FCSTD DOCUMENT  (FreeCAD 0.21R33694 (Git))
Label: box_assembly
License: All rights reserved
LicenseURL: http://en.wikipedia.org/wiki/All_rights_reserved
objects: App::Link×14, App::Part×1
EXTERNAL_REF file=../master_kumiko_box.FCStd obj=Spreadsheet
EXTERNAL_REF file=../parts/box/kumiko_box_floor.FCStd obj=Body032
EXTERNAL_REF file=../parts/box/kumiko_box_wall_long.FCStd obj=Body009
EXTERNAL_REF file=../parts/box/kumiko_box_wall_short.FCStd obj=Body009
EXTERNAL_REF file=../parts/box/kumiko_box_key_miter.FCStd obj=Body014

FEATURE [App::Link] Link  label="SpreadSheet"
  LinkedObject = -> <external ../master_kumiko_box.FCStd>#Spreadsheet
FEATURE [App::Link] Link001  label="floor"
  LinkPlacement = pos=(5.75,5.75,0) rot=(0,0,1;0rad)
  LinkedObject = -> <external ../parts/box/kumiko_box_floor.FCStd>#Body032
  Placement = pos=(5.75,5.75,0) rot=(0,0,1;0rad)
  expr: .Placement.Base.x = <<SpreadSheet>>.box_thickness / 2
  expr: .Placement.Base.y = <<SpreadSheet>>.box_thickness / 2
FEATURE [App::Link] Link002  label="wall_front"
  LinkPlacement = pos=(130,0,2) rot=(0,0,1;1.5708rad)
  LinkedObject = -> <external ../parts/box/kumiko_box_wall_long.FCStd>#Body009
  Placement = pos=(130,0,2) rot=(0,0,1;1.5708rad)
  expr: .Placement.Base.x = <<SpreadSheet>>.box_length
  expr: .Placement.Base.z = <<SpreadSheet>>.floor_edge
  expr: .Placement.Rotation.Angle = 90
FEATURE [App::Link] Link003  label="wall_left"
  LinkPlacement = pos=(0,0,2) rot=(0,0,1;0rad)
  LinkedObject = -> <external ../parts/box/kumiko_box_wall_short.FCStd>#Body009
  Placement = pos=(0,0,2) rot=(0,0,1;0rad)
  expr: .Placement.Base.x = 0
  expr: .Placement.Base.y = 0
  expr: .Placement.Base.z = <<SpreadSheet>>.floor_edge
FEATURE [App::Link] Link004  label="wall_back"
  LinkPlacement = pos=(0,75,2) rot=(0,0,1;4.71239rad)
  LinkedObject = -> <external ../parts/box/kumiko_box_wall_long.FCStd>#Body009
  Placement = pos=(0,75,2) rot=(0,0,1;4.71239rad)
  expr: .Placement.Base.x = 0
  expr: .Placement.Base.y = <<SpreadSheet>>.box_width
  expr: .Placement.Base.z = <<SpreadSheet>>.floor_edge
  expr: .Placement.Rotation.Angle = 270
FEATURE [App::Link] Link005  label="wall_right"
  LinkPlacement = pos=(130,75,2) rot=(0,0,1;3.14159rad)
  LinkedObject = -> <external ../parts/box/kumiko_box_wall_short.FCStd>#Body009
  Placement = pos=(130,75,2) rot=(0,0,1;3.14159rad)
  expr: .Placement.Base.x = <<SpreadSheet>>.box_length
  expr: .Placement.Base.y = <<SpreadSheet>>.box_width
  expr: .Placement.Base.z = <<SpreadSheet>>.floor_edge
  expr: .Placement.Rotation.Angle = 180
FEATURE [App::Link] Link006  label="miter_key_a"
  LinkPlacement = pos=(0,0,9) rot=(0,0,1;0rad)
  LinkedObject = -> <external ../parts/box/kumiko_box_key_miter.FCStd>#Body014
  Placement = pos=(0,0,9) rot=(0,0,1;0rad)
  expr: .Placement.Base.x = 0
  expr: .Placement.Base.z = <<SpreadSheet>>.floor_edge + (<<SpreadSheet>>.lid_height - <<SpreadSheet>>.kumiko_thickness) / 2
FEATURE [App::Link] Link007  label="miter_key_b"
  LinkPlacement = pos=(0,0,33) rot=(0,0,1;0rad)
  LinkedObject = -> <external ../parts/box/kumiko_box_key_miter.FCStd>#Body014
  Placement = pos=(0,0,33) rot=(0,0,1;0rad)
  expr: .Placement.Base.z = <<SpreadSheet>>.box_height - <<SpreadSheet>>.lid_height - (<<SpreadSheet>>.lid_height + <<SpreadSheet>>.kumiko_thickness) / 2
FEATURE [App::Link] Link008  label="miter_key_c"
  LinkPlacement = pos=(130,0,9) rot=(0,0,1;1.5708rad)
  LinkedObject = -> <external ../parts/box/kumiko_box_key_miter.FCStd>#Body014
  Placement = pos=(130,0,9) rot=(0,0,1;1.5708rad)
  expr: .Placement.Base.x = <<SpreadSheet>>.box_length
  expr: .Placement.Base.z = <<SpreadSheet>>.floor_edge + (<<SpreadSheet>>.lid_height - <<SpreadSheet>>.kumiko_thickness) / 2
  expr: .Placement.Rotation.Angle = 90
FEATURE [App::Link] Link009  label="miter_key_d"
  LinkPlacement = pos=(130,0,33) rot=(0,0,1;1.5708rad)
  LinkedObject = -> <external ../parts/box/kumiko_box_key_miter.FCStd>#Body014
  Placement = pos=(130,0,33) rot=(0,0,1;1.5708rad)
  expr: .Placement.Base.x = <<SpreadSheet>>.box_length
  expr: .Placement.Base.z = <<SpreadSheet>>.box_height - <<SpreadSheet>>.lid_height - (<<SpreadSheet>>.lid_height + <<SpreadSheet>>.kumiko_thickness) / 2
  expr: .Placement.Rotation.Angle = 90
FEATURE [App::Link] Link010  label="miter_key_e"
  LinkPlacement = pos=(130,75,9) rot=(0,0,1;3.14159rad)
  LinkedObject = -> <external ../parts/box/kumiko_box_key_miter.FCStd>#Body014
  Placement = pos=(130,75,9) rot=(0,0,1;3.14159rad)
  expr: .Placement.Base.x = <<SpreadSheet>>.box_length
  expr: .Placement.Base.y = <<SpreadSheet>>.box_width
  expr: .Placement.Base.z = <<SpreadSheet>>.floor_edge + (<<SpreadSheet>>.lid_height - <<SpreadSheet>>.kumiko_thickness) / 2
FEATURE [App::Link] Link011  label="miter_key_f"
  LinkPlacement = pos=(130,75,33) rot=(0,0,1;3.14159rad)
  LinkedObject = -> <external ../parts/box/kumiko_box_key_miter.FCStd>#Body014
  Placement = pos=(130,75,33) rot=(0,0,1;3.14159rad)
  expr: .Placement.Base.x = <<SpreadSheet>>.box_length
  expr: .Placement.Base.y = <<SpreadSheet>>.box_width
  expr: .Placement.Base.z = <<SpreadSheet>>.box_height - <<SpreadSheet>>.lid_height - (<<SpreadSheet>>.lid_height + <<SpreadSheet>>.kumiko_thickness) / 2
FEATURE [App::Link] Link012  label="miter_key_g"
  LinkPlacement = pos=(0,75,9) rot=(0,0,1;4.71239rad)
  LinkedObject = -> <external ../parts/box/kumiko_box_key_miter.FCStd>#Body014
  Placement = pos=(0,75,9) rot=(0,0,1;4.71239rad)
  expr: .Placement.Base.y = <<SpreadSheet>>.box_width
  expr: .Placement.Base.z = <<SpreadSheet>>.floor_edge + (<<SpreadSheet>>.lid_height - <<SpreadSheet>>.kumiko_thickness) / 2
FEATURE [App::Link] Link013  label="miter_key_h"
  LinkPlacement = pos=(0,75,33) rot=(0,0,1;4.71239rad)
  LinkedObject = -> <external ../parts/box/kumiko_box_key_miter.FCStd>#Body014
  Placement = pos=(0,75,33) rot=(0,0,1;4.71239rad)
  expr: .Placement.Base.y = <<SpreadSheet>>.box_width
  expr: .Placement.Base.z = <<SpreadSheet>>.box_height - <<SpreadSheet>>.lid_height - (<<SpreadSheet>>.lid_height + <<SpreadSheet>>.kumiko_thickness) / 2
FEATURE [App::Part] Part  label="box"
  Group = -> [Link001,Link004,Link003,Link006,Link007,Link008,Link005,Link002,Link009,Link010,Link011,Link012,Link013]
  Origin = -> Origin

RESOLVED EXTERNAL PARTS (link-assembly join: the EXTERNAL_REF files above that resolve inside this repo's crawl, each included once):
---- part ../master_kumiko_box.FCStd = doc fcstd_d57fc246fb5e ----
FCSTD DOCUMENT  (FreeCAD 0.21R33771 (Git))
Label: master_kumiko_box
License: All rights reserved
LicenseURL: https://en.wikipedia.org/wiki/All_rights_reserved
objects: App::Link×3, App::Part×2, Spreadsheet::Sheet×1
EXTERNAL_REF file=assembly/box_assembly.FCStd obj=Part
EXTERNAL_REF file=assembly/lid_assembly.FCStd obj=Part
EXTERNAL_REF file=assembly/kumiko_assembly.FCStd obj=Part001

FEATURE [Spreadsheet::Sheet] Spreadsheet  label="SpreadSheet"
  cells = A1='name; B1='value; C1='calc (y/n); A2='box_length; B2(box_length)=130; C2='n; A3='box_width; B3(box_width)==B2 / 2 + B5 - B13 / 2; C3='n; A4='box_height; B4(box_height)=60; C4='y; A5='box_thickness; B5(box_thickness)=11.5; C5='y; A7='lid_height; B7(lid_height)==B8 * 17 / 8.5; C7='y; A8='lid_frame_width; B8(lid_frame_width)==B5 - B13; C8='y; A9='lid_lip_width; B9(lid_lip_width)==B5 - B8; C9='y; A10='lid_lip_height; B10(lid_lip_hight)=3; C10='y; A12='kumiko_hight; B12(kumiko_hight)==B7 * 11 / 17; C12='y; A13='kumiko_thickness; B13(kumiko_thickness)=3; C13='n; A14='kumiko_grid_size; B14(kumiko_grid_size)==(B2 - 2 * B8 - B13) / 4; C14='y; A16='box_wall_height; B16(box_wall_height)==B4 - B7 - B18; C16='y; A18='floor_edge; B18(floor_edge)=2; C18='n; A20='cnc_spacing; B20(cnc_spacing)=0; C20='y
FEATURE [App::Link] Link  label="box"
  LinkedObject = -> <external assembly/box_assembly.FCStd>#Part
FEATURE [App::Link] Link001  label="lid"
  LinkPlacement = pos=(0,0,43) rot=(0,0,1;0rad)
  LinkedObject = -> <external assembly/lid_assembly.FCStd>#Part
  Placement = pos=(0,0,43) rot=(0,0,1;0rad)
  expr: .Placement.Base.z = <<SpreadSheet>>.box_height - <<SpreadSheet>>.lid_height
FEATURE [App::Link] Link002  label="kumiko_assembly"
  LinkPlacement = pos=(8.5,8.5,49) rot=(0,0,1;0rad)
  LinkedObject = -> <external assembly/kumiko_assembly.FCStd>#Part001
  Placement = pos=(8.5,8.5,49) rot=(0,0,1;0rad)
  expr: .Placement.Base.x = <<SpreadSheet>>.lid_frame_width
  expr: .Placement.Base.y = <<SpreadSheet>>.lid_frame_width
  expr: .Placement.Base.z = <<SpreadSheet>>.box_height - Spreadsheet.kumiko_hight
FEATURE [App::Part] Part  label="lid_complete"
  Group = -> [Link002,Link001]
  Origin = -> Origin
FEATURE [App::Part] Part001  label="kumiko_box_complete"
  Group = -> [Part,Link]
  Origin = -> Origin001
---- part ../parts/box/kumiko_box_floor.FCStd = doc fcstd_ba5c48548d76 ----
FCSTD DOCUMENT  (FreeCAD 0.21R33771 (Git))
Label: kumiko_box_floor
License: All rights reserved
LicenseURL: https://en.wikipedia.org/wiki/All_rights_reserved
objects: Path::FeaturePython×4, Part::FeaturePython×3, App::DocumentObjectGroup×3, Sketcher::SketchObject×2, PartDesign::Pad×2, App::Link×1, PartDesign::Body×1, App::FeaturePython×1, Mesh::FeaturePython×1
note: 12 computed .brp shape members not serialized (recipe doc carries the construction recipe); baked Part::Feature solids carry a one-line shape summary decoded from their .brp
EXTERNAL_REF file=../../master_kumiko_box.FCStd obj=Spreadsheet

FEATURE [App::Link] Link  label="SpreadSheet"
  LinkedObject = -> <external ../../master_kumiko_box.FCStd>#Spreadsheet
FEATURE [Sketcher::SketchObject] Sketch  label="ground_pad_drawing"
  FullyConstrained = true
  MapMode = 5
  Support = -> [XY_Plane043]
  expr: Constraints[10] = <<SpreadSheet>>.box_width - 2 * <<SpreadSheet>>.box_thickness
  expr: Constraints[11] = <<SpreadSheet>>.box_length - 2 * <<SpreadSheet>>.box_thickness
  expr: Constraints[8] = <<SpreadSheet>>.box_thickness / 2
  expr: Constraints[9] = <<SpreadSheet>>.box_thickness / 2
  sketch-geometry (4):
    g0: LineSegment StartX=5.75 StartY=5.75 StartZ=0 EndX=112.75 EndY=5.75 EndZ=0
    g1: LineSegment StartX=112.75 StartY=5.75 StartZ=0 EndX=112.75 EndY=57.75 EndZ=0
    g2: LineSegment StartX=112.75 StartY=57.75 StartZ=0 EndX=5.75 EndY=57.75 EndZ=0
    g3: LineSegment StartX=5.75 StartY=57.75 StartZ=0 EndX=5.75 EndY=5.75 EndZ=0
  constraints (12):
    c: Coincident(g0,g1)
    c: Coincident(g1,g2)
    c: Coincident(g2,g3)
    c: Coincident(g3,g0)
    c: Horizontal(g0)
    c: Horizontal(g2)
    c: Vertical(g1)
    c: Vertical(g3)
    c: DistanceX(g-1,g0) = 5.75
    c: DistanceY(g-1,g0) = 5.75
    c: DistanceY(g3,g3) = 52
    c: DistanceX(g2,g2) = 107
FEATURE [PartDesign::Pad] Pad  label="ground_pad"
  Direction = (0,0,1)
  Length = 5.75
  Length2 = 10
  Profile = -> Sketch
  ReferenceAxis = -> Sketch [N_Axis]
  Type = 0
  expr: Length = <<SpreadSheet>>.box_thickness / 2
FEATURE [Sketcher::SketchObject] Sketch001  label="half_lap_joint_drawing"
  FullyConstrained = true
  MapMode = 5
  Placement = pos=(0,0,5.75) rot=(0,0,1;0rad)
  Support = -> [Pad]
  expr: Constraints[10] = <<SpreadSheet>>.box_width - <<SpreadSheet>>.box_thickness
  expr: Constraints[9] = <<SpreadSheet>>.box_length - <<SpreadSheet>>.box_thickness
  sketch-geometry (4):
    g0: LineSegment StartX=0 StartY=0 StartZ=0 EndX=118.5 EndY=0 EndZ=0
    g1: LineSegment StartX=118.5 StartY=0 StartZ=0 EndX=118.5 EndY=63.5 EndZ=0
    g2: LineSegment StartX=118.5 StartY=63.5 StartZ=0 EndX=0 EndY=63.5 EndZ=0
    g3: LineSegment StartX=0 StartY=63.5 StartZ=0 EndX=0 EndY=0 EndZ=0
  constraints (12):
    c: Coincident(g0,g1)
    c: Coincident(g1,g2)
    c: Coincident(g2,g3)
    c: Coincident(g3,g0)
    c: Horizontal(g0)
    c: Horizontal(g2)
    c: Vertical(g1)
    c: Vertical(g3)
    c: PointOnObject(g0,g-1)
    c: DistanceX(g2,g2) = 118.5
    c: DistanceY(g1,g1) = 63.5
    c: DistanceX(g-1,g0) = 0
FEATURE [PartDesign::Pad] Pad001  label="half_lap_jount"
  BaseFeature = -> Pad
  Direction = (0,0,1)
  Length = 5.75
  Length2 = 10
  Profile = -> Sketch001
  ReferenceAxis = -> Sketch001 [N_Axis]
  Type = 0
  expr: Length = <<SpreadSheet>>.box_thickness / 2
FEATURE [PartDesign::Body] Body032  label="floor_body"
  Group = -> [Sketch,Pad,Sketch001,Pad001]
  Origin = -> Origin043
  Placement = pos=(0,63.5,0) rot=(1,0,0;3.14159rad)
  Tip = -> Pad001
  expr: .Placement.Base.x = 0
  expr: .Placement.Base.y = <<SpreadSheet>>.box_width - <<SpreadSheet>>.box_thickness
  expr: .Placement.Base.z = 0
FEATURE [App::FeaturePython] SetupSheet  # Path/CAM operation (typed FeaturePython)
  ClearanceHeightExpression = OpStockZMax+SetupSheet.ClearanceHeightOffset
  ClearanceHeightOffset = 5
  CoolantMode = 0
  CoolantModes = None | Flood | Mist
  FinalDepthExpression = OpFinalDepth
  HorizRapid = 0
  SafeHeightExpression = OpStockZMax+SetupSheet.SafeHeightOffset
  SafeHeightOffset = 3
  StartDepthExpression = OpStartDepth
  StepDownExpression = OpToolDiameter
  VertRapid = 0
FEATURE [Part::FeaturePython] Clone  label="Model-floor_body"  # Draft clone (typed FeaturePython)
  AttacherType = Attacher::AttachEngine3D
  Fuse = false
  Objects = -> [Body032]
  PathResource = Model
  Placement = pos=(0,63.5,0) rot=(1,0,0;3.14159rad)
  Scale = (1,1,1)
FEATURE [App::DocumentObjectGroup] Model
  Group = -> [Clone]
FEATURE [Part::FeaturePython] Stock  # WARN: FeaturePython — macro-defined, semantics opaque (R4)
  Base = -> Model
  ExtXneg = 3
  ExtXpos = 3
  ExtYneg = 3
  ExtYpos = 3
  ExtZneg = 0
  ExtZpos = 0
  Placement = pos=(0,0,-11.5) rot=(0,0,1;0rad)
  StockType = FromBase
FEATURE [Part::FeaturePython] ToolBit001  label="FREES_5mm"  # Path/CAM toolbit (typed FeaturePython)
  BitPropertyNames = Chipload | CuttingEdgeHeight | Diameter | Flutes | Length | Material | ShankDiameter | SpindleDirection
  BitShape = /Applications/FreeCAD.app/Contents/Resources/Mod/Path/Tools/Shape/endmill.fcstd
  Chipload = 0
  CuttingEdgeHeight = 13
  Diameter = 5
  File = <userpath>/Library/Application Support/FreeCAD/Macro/FREES_5mm.fctb
  Flutes = 0
  Length = 57
  Material = 0
  ShankDiameter = 6
  ShapeName = endmill
  SpindleDirection = 0
FEATURE [Path::FeaturePython] FREES_5mm  label="FREES_5mm001"  # Path/CAM operation (typed FeaturePython)
  HorizFeed = 1
  HorizRapid = 0
  SpindleDir = 0
  SpindleSpeed = 4
  Tool = -> ToolBit001
  ToolNumber = 2
  VertFeed = 0.5
  VertRapid = 0
  expr: HorizRapid = SetupSheet.HorizRapid
  expr: VertRapid = SetupSheet.VertRapid
FEATURE [App::DocumentObjectGroup] Tools
  Group = -> [FREES_5mm]
FEATURE [Path::FeaturePython] Profile  # Path/CAM operation (typed FeaturePython)
  Active = true
  AreaParams:
    Tolerance = 1e-07
    FitArcs = True
    Simplify = False
    CleanDistance = 0.0
    Accuracy = 0.01
    Unit = 1.0
    MinArcPoints = 4
    MaxArcPoints = 100
    ClipperScale = 10000000.0
    Fill = 0
    Coplanar = 0
    Reorient = True
    Outline = False
    Explode = False
    OpenMode = 0
    Deflection = 0.01
    SubjectFill = 0
    ClipFill = 0
    Offset = 2.5
    ExtraPass = 0
    Stepover = 0.0
    LastStepover = 0.0
    JoinType = 0
    EndType = 0
    MiterLimit = 2.0
    RoundPrecision = 0.0
    PocketMode = 0
    ToolRadius = 1.0
    PocketExtraOffset = 0.0
    PocketStepover = 0.0
    PocketLastStepover = 0.0
    FromCenter = False
    Angle = 45.0
    AngleShift = 0.0
    Shift = 0.0
    Thicken = False
    SectionCount = -1
    Stepdown = 1.0
    SectionOffset = 0.0
    SectionTolerance = 1e-07
    SectionMode = 2
    Project = False
  Base = -> [Clone]
  ClearanceHeight = 5
  CoolantMode = 0
  CycleTime = 01:16:33
  Direction = 1
  FinalDepth = -11.5
  HandleMultipleFeatures = 0
  JoinType = 0
  MiterLimit = 0.1
  OffsetExtra = 0
  OpFinalDepth = -11.5
  OpStartDepth = 7.1e-15
  OpStockZMax = 0
  OpStockZMin = -11.5
  OpToolDiameter = 5
  PathParams = {'orientation': 0, 'feedrate': 1.0, 'feedrate_v': 0.5, 'verbose': True, 'resume_height': 3.0, 'retraction': 5.0, 'return_end': True, 'preamble': False, 'start': Vector (0.0, 0.0, 0.0)}
  SafeHeight = 3
  Side = 0
  SplitArcs = false
  StartDepth = 7.1e-15
  StartPoint = (0,0,0)
  StepDown = 1
  ToolController = -> FREES_5mm
  UseComp = true
  UseStartPoint = true
  processCircles = false
  processHoles = false
  processPerimeter = true
  expr: ClearanceHeight = OpStockZMax + SetupSheet.ClearanceHeightOffset
  expr: FinalDepth = OpFinalDepth
  expr: SafeHeight = OpStockZMax + SetupSheet.SafeHeightOffset
  expr: StartDepth = OpStartDepth
  expr: StepDown = 1
FEATURE [Path::FeaturePython] Pocket_Shape  # Path/CAM operation (typed FeaturePython)
  Active = true
  AreaParams:
    Tolerance = 1e-07
    FitArcs = True
    Simplify = False
    CleanDistance = 0.0
    Accuracy = 0.01
    Unit = 1.0
    MinArcPoints = 4
    MaxArcPoints = 100
    ClipperScale = 10000000.0
    Fill = 0
    Coplanar = 0
    Reorient = True
    Outline = False
    Explode = False
    OpenMode = 0
    Deflection = 0.01
    SubjectFill = 0
    ClipFill = 0
    Offset = 0.0
    ExtraPass = 0
    Stepover = 0.0
    LastStepover = 0.0
    JoinType = 0
    EndType = 0
    MiterLimit = 2.0
    RoundPrecision = 0.0
    PocketMode = 2
    ToolRadius = 2.5
    PocketExtraOffset = 0.0
    PocketStepover = 2.0
    PocketLastStepover = 0.0
    FromCenter = True
    Angle = 45.0
    AngleShift = 0.0
    Shift = 0.0
    Thicken = False
    SectionCount = -1
    Stepdown = 1.0
    SectionOffset = 0.0
    SectionTolerance = 1e-07
    SectionMode = 2
    Project = False
  Base = -> [Clone]
  ClearanceHeight = 5
  CoolantMode = 0
  CutMode = 0
  CycleTime = 02:11:12
  ExtensionCorners = true
  ExtensionFeature = -> [Clone]
  ExtensionLengthDefault = 2.5
  ExtraOffset = 0
  FinalDepth = -5.75
  FinishDepth = 0.5
  KeepToolDown = false
  MinTravel = false
  OffsetPattern = 1
  OpFinalDepth = -5.75
  OpStartDepth = 7.1e-15
  OpStockZMax = 0
  OpStockZMin = -11.5
  OpToolDiameter = 5
  PathParams = {'orientation': 1, 'feedrate': 1.0, 'feedrate_v': 0.5, 'verbose': True, 'resume_height': 3.0, 'retraction': 5.0, 'return_end': True, 'preamble': False, 'start': Vector (0.0, 0.0, 0.0)}
  PocketLastStepOver = 0
  SafeHeight = 3
  SplitArcs = false
  StartAt = 0
  StartDepth = 7.1e-15
  StartPoint = (0,0,0)
  StepDown = 1
  StepOver = 40
  ToolController = -> FREES_5mm
  UseOutline = false
  UseStartPoint = true
  ZigZagAngle = 45
  expr: ClearanceHeight = OpStockZMax + SetupSheet.ClearanceHeightOffset
  expr: ExtensionLengthDefault = OpToolDiameter / 2
  expr: FinalDepth = OpFinalDepth
  expr: SafeHeight = OpStockZMax + SetupSheet.SafeHeightOffset
  expr: StartDepth = OpStartDepth
  expr: StepDown = 1
FEATURE [App::DocumentObjectGroup] Operations
  Group = -> [Profile,Pocket_Shape]
FEATURE [Path::FeaturePython] Job  # Path/CAM operation (typed FeaturePython)
  CycleTime = 03:27:45
  Fixtures = G54
  GeometryTolerance = 0.01
  JobType = 0
  LastPostProcessDate = 2024-03-20 12:44:18.073578
  LastPostProcessOutput = <userpath>/Documents/jewelry_kumiko_box/cnc/bin/kumiko_floor-0.nc
  Model = -> Model
  Operations = -> Operations
  OrderOutputBy = 0
  PostProcessor = 14
  PostProcessorOutputFile = <userpath>/Documents/jewelry_kumiko_box/cnc/bin/kumiko_floor.nc
  SetupSheet = -> SetupSheet
  SplitOutput = true
  Stock = -> Stock
  Tools = -> Tools
FEATURE [Mesh::FeaturePython] CutMaterial  # WARN: FeaturePython — macro-defined, semantics opaque (R4)
---- part ../parts/box/kumiko_box_key_miter.FCStd = doc fcstd_dc4a3549b709 ----
FCSTD DOCUMENT  (FreeCAD 0.21R33694 (Git))
Label: kumiko_box_key_miter
License: All rights reserved
LicenseURL: https://en.wikipedia.org/wiki/All_rights_reserved
objects: Sketcher::SketchObject×1, PartDesign::Pad×1, PartDesign::Body×1, App::Link×1
note: 4 computed .brp shape members not serialized (recipe doc carries the construction recipe); baked Part::Feature solids carry a one-line shape summary decoded from their .brp
EXTERNAL_REF file=../../master_kumiko_box.FCStd obj=Spreadsheet

FEATURE [Sketcher::SketchObject] Sketch027  label="miter_key_drawing"
  FullyConstrained = true
  MapMode = 5
  Support = -> [XY_Plane016]
  expr: Constraints[6] = <<SpreadSheet>>.lid_frame_width
  expr: Constraints[7] = 0
  expr: Constraints[8] = 0
  sketch-geometry (3):
    g0: LineSegment StartX=0 StartY=8.5 StartZ=0 EndX=0 EndY=0 EndZ=0
    g1: LineSegment StartX=0 StartY=0 StartZ=0 EndX=8.5 EndY=0 EndZ=0
    g2: LineSegment StartX=8.5 StartY=0 StartZ=0 EndX=0 EndY=8.5 EndZ=0
  constraints (9):
    c: Vertical(g0)
    c: Coincident(g1,g0)
    c: Horizontal(g1)
    c: Coincident(g2,g1)
    c: Coincident(g2,g0)
    c: Equal(g0,g1)
    c: DistanceX(g1,g1) = 8.5
    c: DistanceX(g-1,g0) = 0
    c: DistanceY(g0,g-1) = 0
FEATURE [PartDesign::Pad] Pad012  label="miter_key_extrude"
  Direction = (0,0,1)
  Length = 3
  Length2 = 10
  Profile = -> Sketch027
  ReferenceAxis = -> Sketch027 [N_Axis]
  Type = 0
  expr: Length = <<SpreadSheet>>.kumiko_thickness
FEATURE [PartDesign::Body] Body014  label="miter_key"
  Group = -> [Sketch027,Pad012]
  Origin = -> Origin016
  Tip = -> Pad012
  expr: .Placement.Base.x = 0
  expr: .Placement.Base.y = 0
  expr: .Placement.Base.z = 0
  expr: .Placement.Rotation.Angle = 0
  expr: .Placement.Rotation.Axis.x = 0
  expr: .Placement.Rotation.Axis.y = 0
  expr: .Placement.Rotation.Axis.z = 1
FEATURE [App::Link] Link  label="SpreadSheet"
  LinkedObject = -> <external ../../master_kumiko_box.FCStd>#Spreadsheet
---- part ../parts/box/kumiko_box_wall_long.FCStd = doc fcstd_1593c2cb809c ----
FCSTD DOCUMENT  (FreeCAD 0.21R33694 (Git))
Label: kumiko_box_wall_long
License: All rights reserved
LicenseURL: https://en.wikipedia.org/wiki/All_rights_reserved
objects: Sketcher::SketchObject×3, PartDesign::Pocket×2, PartDesign::Pad×1, PartDesign::Mirrored×1, PartDesign::Body×1, App::Link×1
note: 11 computed .brp shape members not serialized (recipe doc carries the construction recipe); baked Part::Feature solids carry a one-line shape summary decoded from their .brp
EXTERNAL_REF file=../../master_kumiko_box.FCStd obj=Spreadsheet

FEATURE [Sketcher::SketchObject] Sketch014  label="profile_drawing"
  FullyConstrained = true
  MapMode = 5
  Placement = pos=(0,0,0) rot=(1,0,0;1.5708rad)
  Support = -> [XZ_Plane009]
  expr: Constraints[12] = <<SpreadSheet>>.box_thickness / 2
  expr: Constraints[24] = <<SpreadSheet>>.box_thickness / 2
  expr: Constraints[25] = <<SpreadSheet>>.lid_lip_hight
  expr: Constraints[26] = <<SpreadSheet>>.box_thickness / 2
  expr: Constraints[27] = <<SpreadSheet>>.box_thickness - <<SpreadSheet>>.floor_edge
  expr: Constraints[28] = <<SpreadSheet>>.box_wall_height
  expr: Constraints[29] = <<SpreadSheet>>.box_thickness
  expr: Constraints[5] = <<SpreadSheet>>.box_thickness
  expr: Constraints[7] = 0
  sketch-geometry (10):
    g0: LineSegment StartX=0 StartY=41 StartZ=0 EndX=0 EndY=0 EndZ=0
    g1: LineSegment StartX=0 StartY=0 StartZ=0 EndX=11.5 EndY=0 EndZ=0
    g2: LineSegment StartX=11.5 StartY=0 StartZ=0 EndX=11.5 EndY=3.75 EndZ=0
    g3: LineSegment StartX=11.5 StartY=3.75 StartZ=0 EndX=5.75 EndY=3.75 EndZ=0
    g4: LineSegment StartX=5.75 StartY=3.75 StartZ=0 EndX=5.75 EndY=9.5 EndZ=0
    g5: LineSegment StartX=5.75 StartY=9.5 StartZ=0 EndX=11.5 EndY=9.5 EndZ=0
    g6: LineSegment StartX=0 StartY=41 StartZ=0 EndX=5.75 EndY=41 EndZ=0
    g7: LineSegment StartX=5.75 StartY=44 StartZ=0 EndX=11.5 EndY=44 EndZ=0
    g8: LineSegment StartX=11.5 StartY=44 StartZ=0 EndX=11.5 EndY=9.5 EndZ=0
    g9: LineSegment StartX=5.75 StartY=44 StartZ=0 EndX=5.75 EndY=41 EndZ=0
  constraints (30):
    c: Vertical(g0)
    c: Coincident(g1,g0)
    c: Horizontal(g1)
    c: Coincident(g2,g1)
    c: Vertical(g2)
    c: DistanceX(g1,g1) = 11.5
    c: DistanceX(g-1,g0) = 0
    c: DistanceY(g0,g-1) = 0
    c: Coincident(g3,g2)
    c: Horizontal(g3)
    c: Coincident(g4,g3)
    c: Vertical(g4)
    c: DistanceY(g4,g4) = 5.75
    c: Coincident(g5,g4)
    c: Horizontal(g5)
    c: Coincident(g6,g0)
    c: Horizontal(g6)
    c: Horizontal(g7)
    c: Coincident(g8,g7)
    c: Coincident(g8,g5)
    c: Vertical(g8)
    c: Coincident(g9,g7)
    c: Coincident(g9,g6)
    c: Vertical(g9)
    c: DistanceX(g7,g7) = 5.75
    c: DistanceY(g9,g9) = 3
    c: DistanceX(g5,g5) = 5.75
    c: DistanceY(g1,g5) = 9.5
    c: DistanceY(g0,g0) = 41
    c: DistanceX(g0,g7) = 11.5
FEATURE [PartDesign::Pad] Pad007  label="wall_profile_extrusion"
  Direction = (0,-1,-2e-16)
  Length = 65
  Length2 = 10
  Placement = pos=(0,0,0) rot=(1,0,0;1.5708rad)
  Profile = -> Sketch014
  ReferenceAxis = -> Sketch014 [N_Axis]
  Reversed = true
  Type = 0
  expr: Length = <<SpreadSheet>>.box_length / 2
FEATURE [Sketcher::SketchObject] Sketch015  label="miter_drawing"
  FullyConstrained = true
  MapMode = 5
  Placement = pos=(0,0,0) rot=(1,0,0;3.14159rad)
  Support = -> [Pad007]
  expr: Constraints[4] = <<SpreadSheet>>.box_thickness
  expr: Constraints[7] = <<SpreadSheet>>.box_thickness
  sketch-geometry (3):
    g0: LineSegment StartX=0 StartY=0 StartZ=0 EndX=11.5 EndY=0 EndZ=0
    g1: LineSegment StartX=11.5 StartY=0 StartZ=0 EndX=11.5 EndY=-11.5 EndZ=0
    g2: LineSegment StartX=0 StartY=0 StartZ=0 EndX=11.5 EndY=-11.5 EndZ=0
  constraints (8):
    c: Coincident(g0,g-1)
    c: PointOnObject(g0,g-1)
    c: Coincident(g1,g0)
    c: Vertical(g1)
    c: DistanceX(g0,g0) = 11.5
    c: Coincident(g2,g0)
    c: Coincident(g2,g1)
    c: DistanceY(g1,g0) = 11.5
FEATURE [PartDesign::Pocket] Pocket006  label="miter_cut"
  BaseFeature = -> Pad007
  Direction = (0,-2e-16,1)
  Length = 60
  Length2 = 5
  Placement = pos=(0,0,0) rot=(1,0,0;1.5708rad)
  Profile = -> Sketch015
  ReferenceAxis = -> Sketch015 [N_Axis]
  Type = 0
  expr: Length = <<SpreadSheet>>.box_height
FEATURE [Sketcher::SketchObject] Sketch016  label="miter_key_drawing"
  FullyConstrained = true
  MapMode = 5
  Placement = pos=(0,0,0) rot=(0.678598,-0.281085,0.678598;2.59356rad)
  Support = -> [Pocket006]
  expr: Constraints[10] = <<SpreadSheet>>.lid_frame_width * sqrt(2) / 2
  expr: Constraints[19] = -(<<SpreadSheet>>.lid_height / 2 + <<SpreadSheet>>.kumiko_thickness / 2)
  expr: Constraints[20] = -(<<SpreadSheet>>.box_wall_height - <<SpreadSheet>>.lid_height / 2 - <<SpreadSheet>>.kumiko_thickness / 2)
  expr: Constraints[21] = -(<<SpreadSheet>>.box_wall_height - <<SpreadSheet>>.lid_height / 2 + <<SpreadSheet>>.kumiko_thickness / 2)
  expr: Constraints[8] = -(<<SpreadSheet>>.lid_height / 2 - <<SpreadSheet>>.kumiko_thickness / 2)
  sketch-geometry (8):
    g0: LineSegment StartX=10 StartY=-6.01041 StartZ=0 EndX=7 EndY=-6.01041 EndZ=0
    g1: LineSegment StartX=7 StartY=-6.01041 StartZ=0 EndX=7 EndY=0 EndZ=0
    g2: LineSegment StartX=7 StartY=0 StartZ=0 EndX=10 EndY=0 EndZ=0
    g3: LineSegment StartX=10 StartY=0 StartZ=0 EndX=10 EndY=-6.01041 EndZ=0
    g4: LineSegment StartX=31 StartY=-6.01041 StartZ=0 EndX=34 EndY=-6.01041 EndZ=0
    g5: LineSegment StartX=34 StartY=-6.01041 StartZ=0 EndX=34 EndY=0 EndZ=0
    g6: LineSegment StartX=34 StartY=0 StartZ=0 EndX=31 EndY=0 EndZ=0
    g7: LineSegment StartX=31 StartY=0 StartZ=0 EndX=31 EndY=-6.01041 EndZ=0
  constraints (24):
    c: Coincident(g0,g1)
    c: Coincident(g1,g2)
    c: Coincident(g2,g3)
    c: Coincident(g3,g0)
    c: Horizontal(g0)
    c: Horizontal(g2)
    c: Vertical(g1)
    c: Vertical(g3)
    c: DistanceX(g1,g-1) = -7
    c: DistanceY(g1,g-1) = 0
    c: DistanceY(g3,g3) = 6.01041
    c: Coincident(g4,g5)
    c: Coincident(g5,g6)
    c: Coincident(g6,g7)
    c: Coincident(g7,g4)
    c: Horizontal(g4)
    c: Horizontal(g6)
    c: Vertical(g5)
    c: Vertical(g7)
    c: DistanceX(g2,g-1) = -10
    c: DistanceX(g6,g-1) = -31
    c: DistanceX(g5,g-1) = -34
    c: Equal(g3,g7)
    c: DistanceY(g6,g-1) = 0
FEATURE [PartDesign::Pocket] Pocket007  label="miter_key_slot"
  BaseFeature = -> Pocket006
  Direction = (-0.707107,0.707107,1e-16)
  Length = 5
  Length2 = 5
  Placement = pos=(0,0,0) rot=(1,0,0;1.5708rad)
  Profile = -> Sketch016
  ReferenceAxis = -> Sketch016 [N_Axis]
  Type = 1
FEATURE [PartDesign::Mirrored] Mirrored003  label="wall_mirror"
  BaseFeature = -> Pocket007
  MirrorPlane = -> Pocket007 [Face4]
  Originals = -> [Pad007,Pocket006,Pocket007]
  Placement = pos=(0,0,0) rot=(1,0,0;1.5708rad)
  Refine = true
FEATURE [PartDesign::Body] Body009  label="wall_long_body"
  Group = -> [Sketch014,Pad007,Sketch015,Pocket006,Sketch016,Pocket007,Mirrored003]
  Origin = -> Origin009
  Placement = pos=(130,0,0) rot=(0,0,1;1.5708rad)
  Tip = -> Mirrored003
  expr: .Placement.Base.x = <<SpreadSheet>>.box_length
  expr: .Placement.Rotation.Angle = 90
FEATURE [App::Link] Link  label="SpreadSheet"
  LinkedObject = -> <external ../../master_kumiko_box.FCStd>#Spreadsheet
---- part ../parts/box/kumiko_box_wall_short.FCStd = doc fcstd_0eab396ce7b4 ----
FCSTD DOCUMENT  (FreeCAD 0.21R33694 (Git))
Label: kumiko_box_wall_short
License: All rights reserved
LicenseURL: https://en.wikipedia.org/wiki/All_rights_reserved
objects: Sketcher::SketchObject×3, PartDesign::Pocket×2, PartDesign::Pad×1, PartDesign::Mirrored×1, PartDesign::Body×1, App::Link×1
note: 11 computed .brp shape members not serialized (recipe doc carries the construction recipe); baked Part::Feature solids carry a one-line shape summary decoded from their .brp
EXTERNAL_REF file=../../master_kumiko_box.FCStd obj=Spreadsheet

FEATURE [Sketcher::SketchObject] Sketch014  label="wall_profile_drawing"
  FullyConstrained = true
  MapMode = 5
  Placement = pos=(0,0,0) rot=(1,0,0;1.5708rad)
  Support = -> [XZ_Plane009]
  expr: Constraints[12] = <<SpreadSheet>>.box_thickness / 2
  expr: Constraints[24] = <<SpreadSheet>>.box_thickness / 2
  expr: Constraints[25] = <<SpreadSheet>>.lid_lip_hight
  expr: Constraints[26] = <<SpreadSheet>>.box_thickness / 2
  expr: Constraints[27] = <<SpreadSheet>>.box_thickness - <<SpreadSheet>>.floor_edge
  expr: Constraints[28] = <<SpreadSheet>>.box_wall_height
  expr: Constraints[29] = <<SpreadSheet>>.box_thickness
  expr: Constraints[5] = <<SpreadSheet>>.box_thickness
  expr: Constraints[7] = 0
  sketch-geometry (10):
    g0: LineSegment StartX=0 StartY=41 StartZ=0 EndX=0 EndY=0 EndZ=0
    g1: LineSegment StartX=0 StartY=0 StartZ=0 EndX=11.5 EndY=0 EndZ=0
    g2: LineSegment StartX=11.5 StartY=0 StartZ=0 EndX=11.5 EndY=3.75 EndZ=0
    g3: LineSegment StartX=11.5 StartY=3.75 StartZ=0 EndX=5.75 EndY=3.75 EndZ=0
    g4: LineSegment StartX=5.75 StartY=3.75 StartZ=0 EndX=5.75 EndY=9.5 EndZ=0
    g5: LineSegment StartX=5.75 StartY=9.5 StartZ=0 EndX=11.5 EndY=9.5 EndZ=0
    g6: LineSegment StartX=0 StartY=41 StartZ=0 EndX=5.75 EndY=41 EndZ=0
    g7: LineSegment StartX=5.75 StartY=44 StartZ=0 EndX=11.5 EndY=44 EndZ=0
    g8: LineSegment StartX=11.5 StartY=44 StartZ=0 EndX=11.5 EndY=9.5 EndZ=0
    g9: LineSegment StartX=5.75 StartY=44 StartZ=0 EndX=5.75 EndY=41 EndZ=0
  constraints (30):
    c: Vertical(g0)
    c: Coincident(g1,g0)
    c: Horizontal(g1)
    c: Coincident(g2,g1)
    c: Vertical(g2)
    c: DistanceX(g1,g1) = 11.5
    c: DistanceX(g-1,g0) = 0
    c: DistanceY(g0,g-1) = 0
    c: Coincident(g3,g2)
    c: Horizontal(g3)
    c: Coincident(g4,g3)
    c: Vertical(g4)
    c: DistanceY(g4,g4) = 5.75
    c: Coincident(g5,g4)
    c: Horizontal(g5)
    c: Coincident(g6,g0)
    c: Horizontal(g6)
    c: Horizontal(g7)
    c: Coincident(g8,g7)
    c: Coincident(g8,g5)
    c: Vertical(g8)
    c: Coincident(g9,g7)
    c: Coincident(g9,g6)
    c: Vertical(g9)
    c: DistanceX(g7,g7) = 5.75
    c: DistanceY(g9,g9) = 3
    c: DistanceX(g5,g5) = 5.75
    c: DistanceY(g1,g5) = 9.5
    c: DistanceY(g0,g0) = 41
    c: DistanceX(g0,g7) = 11.5
FEATURE [PartDesign::Pad] Pad007  label="wall_profile_extrusion"
  Direction = (0,-1,-2e-16)
  Length = 37.5
  Length2 = 10
  Placement = pos=(0,0,0) rot=(1,0,0;1.5708rad)
  Profile = -> Sketch014
  ReferenceAxis = -> Sketch014 [N_Axis]
  Reversed = true
  Type = 0
  expr: Length = <<SpreadSheet>>.box_width / 2
FEATURE [Sketcher::SketchObject] Sketch015  label="miter_drawing"
  FullyConstrained = true
  MapMode = 5
  Placement = pos=(0,0,0) rot=(1,0,0;3.14159rad)
  Support = -> [Pad007]
  expr: Constraints[4] = <<SpreadSheet>>.box_thickness
  expr: Constraints[7] = <<SpreadSheet>>.box_thickness
  sketch-geometry (3):
    g0: LineSegment StartX=0 StartY=0 StartZ=0 EndX=11.5 EndY=0 EndZ=0
    g1: LineSegment StartX=11.5 StartY=0 StartZ=0 EndX=11.5 EndY=-11.5 EndZ=0
    g2: LineSegment StartX=0 StartY=0 StartZ=0 EndX=11.5 EndY=-11.5 EndZ=0
  constraints (8):
    c: Coincident(g0,g-1)
    c: PointOnObject(g0,g-1)
    c: Coincident(g1,g0)
    c: Vertical(g1)
    c: DistanceX(g0,g0) = 11.5
    c: Coincident(g2,g0)
    c: Coincident(g2,g1)
    c: DistanceY(g1,g0) = 11.5
FEATURE [PartDesign::Pocket] Pocket006  label="miter_cut"
  BaseFeature = -> Pad007
  Direction = (0,-2e-16,1)
  Length = 60
  Length2 = 5
  Placement = pos=(0,0,0) rot=(1,0,0;1.5708rad)
  Profile = -> Sketch015
  ReferenceAxis = -> Sketch015 [N_Axis]
  Type = 0
  expr: Length = <<SpreadSheet>>.box_height
FEATURE [Sketcher::SketchObject] Sketch016  label="miter_key_drawing"
  FullyConstrained = true
  MapMode = 5
  Placement = pos=(0,0,0) rot=(0.678598,-0.281085,0.678598;2.59356rad)
  Support = -> [Pocket006]
  expr: Constraints[10] = <<SpreadSheet>>.lid_frame_width * sqrt(2) / 2
  expr: Constraints[19] = -(<<SpreadSheet>>.lid_height / 2 + <<SpreadSheet>>.kumiko_thickness / 2)
  expr: Constraints[20] = -(<<SpreadSheet>>.box_wall_height - <<SpreadSheet>>.lid_height / 2 - <<SpreadSheet>>.kumiko_thickness / 2)
  expr: Constraints[21] = -(<<SpreadSheet>>.box_wall_height - <<SpreadSheet>>.lid_height / 2 + <<SpreadSheet>>.kumiko_thickness / 2)
  expr: Constraints[8] = -(<<SpreadSheet>>.lid_height / 2 - <<SpreadSheet>>.kumiko_thickness / 2)
  sketch-geometry (8):
    g0: LineSegment StartX=10 StartY=-6.01041 StartZ=0 EndX=7 EndY=-6.01041 EndZ=0
    g1: LineSegment StartX=7 StartY=-6.01041 StartZ=0 EndX=7 EndY=0 EndZ=0
    g2: LineSegment StartX=7 StartY=0 StartZ=0 EndX=10 EndY=0 EndZ=0
    g3: LineSegment StartX=10 StartY=0 StartZ=0 EndX=10 EndY=-6.01041 EndZ=0
    g4: LineSegment StartX=31 StartY=-6.01041 StartZ=0 EndX=34 EndY=-6.01041 EndZ=0
    g5: LineSegment StartX=34 StartY=-6.01041 StartZ=0 EndX=34 EndY=0 EndZ=0
    g6: LineSegment StartX=34 StartY=0 StartZ=0 EndX=31 EndY=0 EndZ=0
    g7: LineSegment StartX=31 StartY=0 StartZ=0 EndX=31 EndY=-6.01041 EndZ=0
  constraints (24):
    c: Coincident(g0,g1)
    c: Coincident(g1,g2)
    c: Coincident(g2,g3)
    c: Coincident(g3,g0)
    c: Horizontal(g0)
    c: Horizontal(g2)
    c: Vertical(g1)
    c: Vertical(g3)
    c: DistanceX(g1,g-1) = -7
    c: DistanceY(g1,g-1) = 0
    c: DistanceY(g3,g3) = 6.01041
    c: Coincident(g4,g5)
    c: Coincident(g5,g6)
    c: Coincident(g6,g7)
    c: Coincident(g7,g4)
    c: Horizontal(g4)
    c: Horizontal(g6)
    c: Vertical(g5)
    c: Vertical(g7)
    c: DistanceX(g2,g-1) = -10
    c: DistanceX(g6,g-1) = -31
    c: DistanceX(g5,g-1) = -34
    c: Equal(g3,g7)
    c: DistanceY(g6,g-1) = 0
FEATURE [PartDesign::Pocket] Pocket007  label="miter_key_cut"
  BaseFeature = -> Pocket006
  Direction = (-0.707107,0.707107,1e-16)
  Length = 5
  Length2 = 5
  Placement = pos=(0,0,0) rot=(1,0,0;1.5708rad)
  Profile = -> Sketch016
  ReferenceAxis = -> Sketch016 [N_Axis]
  Type = 1
FEATURE [PartDesign::Mirrored] Mirrored003  label="wall_mirror"
  BaseFeature = -> Pocket007
  MirrorPlane = -> Pocket007 [Face4]
  Originals = -> [Pad007,Pocket006,Pocket007]
  Placement = pos=(0,0,0) rot=(1,0,0;1.5708rad)
  Refine = true
FEATURE [PartDesign::Body] Body009  label="wall_short_body"
  Group = -> [Sketch014,Pad007,Sketch015,Pocket006,Sketch016,Pocket007,Mirrored003]
  Origin = -> Origin009
  Tip = -> Mirrored003
FEATURE [App::Link] Link  label="SpreadSheet"
  LinkedObject = -> <external ../../master_kumiko_box.FCStd>#Spreadsheet
